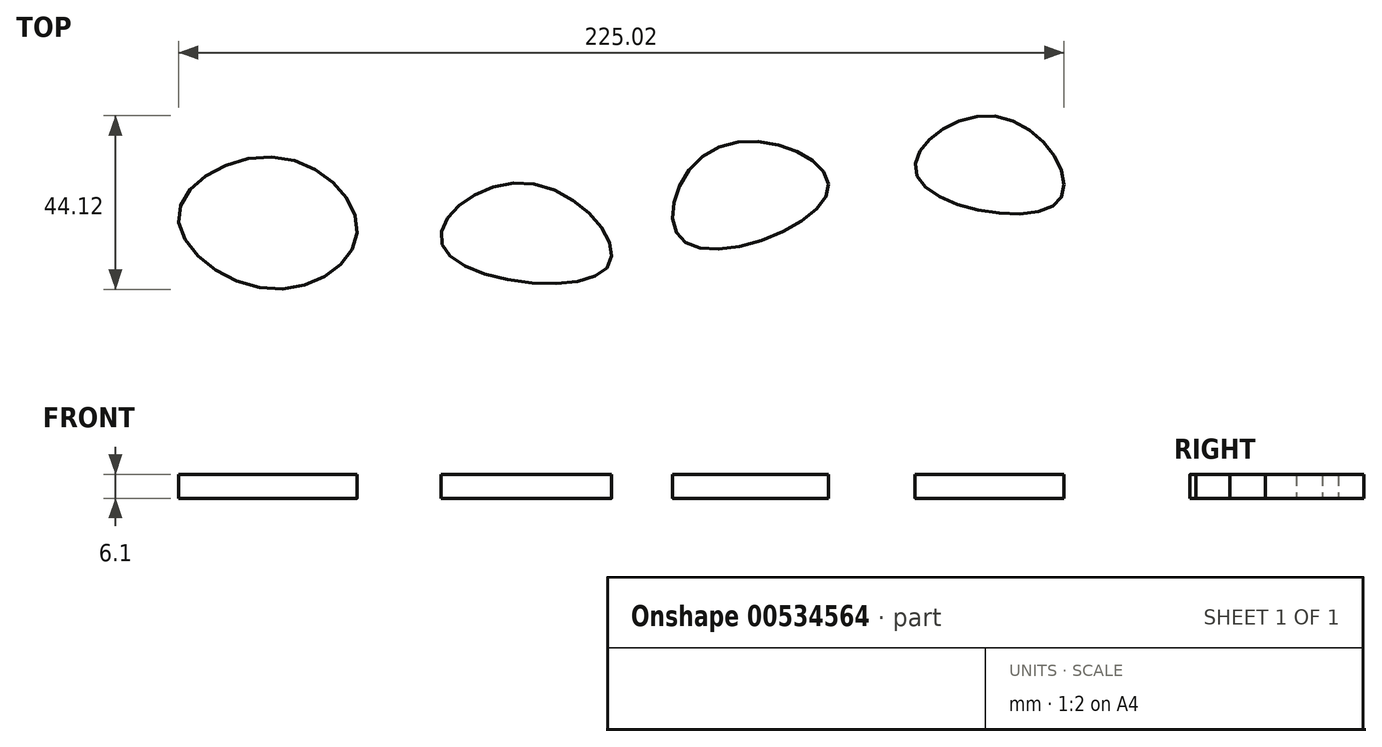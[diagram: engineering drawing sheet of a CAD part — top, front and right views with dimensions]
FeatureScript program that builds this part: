
annotation { "Feature Type Name" : "Feature", "Feature Type Description" : "" }
export const myFeature = defineFeature(function(context is Context, id is Id, definition is map)
    precondition{}
    {
        {
            var Q0;
            Q0=qCreatedBy(makeId("Top.planeOp"),FACE);
            var sketch = newSketch(context, id + "F0", { "sketchPlane" : qUnion([Q0])});
            skFitSpline(sketch, "E0", {"points": [v(0, 0) * mm, v(-20.07, 21.49) * mm, v(-41.52, 5.04) * mm, v(0, 0) * mm]});
            skFitSpline(sketch, "E1", {"points": [v(19.93, 6.36) * mm, v(28.13, 30.6) * mm, v(56.2, 19.83) * mm, v(19.93, 6.36) * mm]});
            skFitSpline(sketch, "E2", {"points": [v(-63.52, 8.87) * mm, v(-83.27, 28.03) * mm, v(-108.85, 13.55) * mm, v(-85.58, -5.4) * mm, v(-63.52, 8.87) * mm]});
            skFitSpline(sketch, "E3", {"points": [v(78.7, 23.33) * mm, v(99.37, 38.43) * mm, v(114.67, 16.9) * mm, v(78.7, 23.33) * mm]});
            skSolve(sketch);
        }
        {
            var Q0;
            Q0 = qSketchRegion(id + "F0", true);
            extrude(context, id + "F1", {"entities" : qUnion([Q0]), "depth" : 6.1 * mm, "offsetDistance" : 25.4 * mm});
        }
    });
